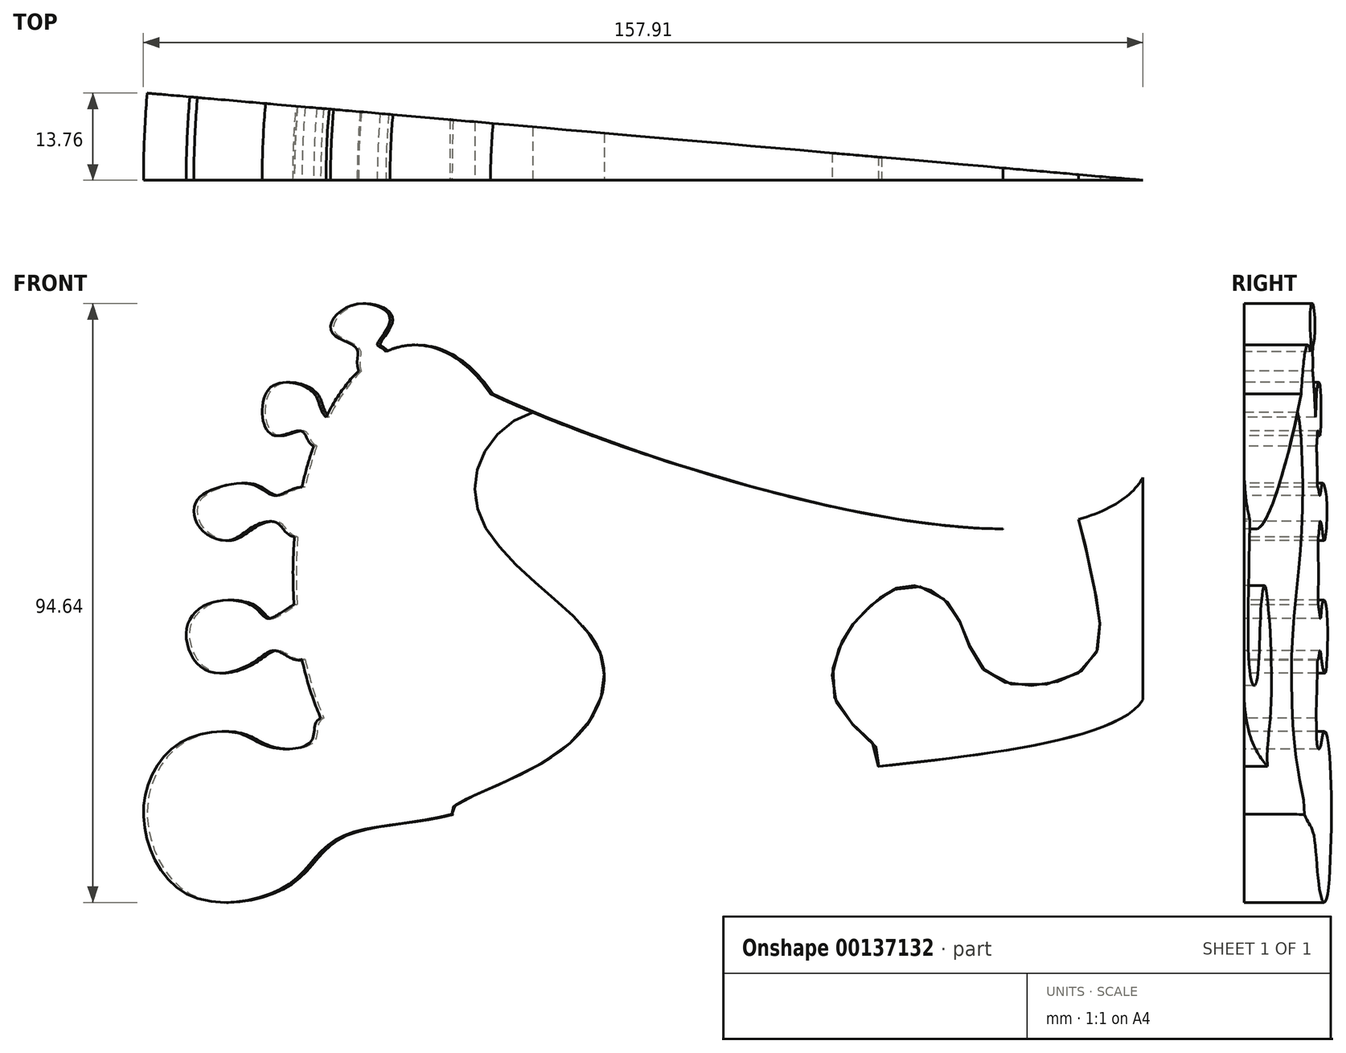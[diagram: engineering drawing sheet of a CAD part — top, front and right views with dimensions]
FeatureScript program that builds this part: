
annotation { "Feature Type Name" : "Feature", "Feature Type Description" : "" }
export const myFeature = defineFeature(function(context is Context, id is Id, definition is map)
    precondition{}
    {
        {
            var Q0;
            Q0=qCreatedBy(makeId("Front.planeOp"),FACE);
            var sketch = newSketch(context, id + "F0", { "sketchPlane" : qUnion([Q0])});
            skLineSegment(sketch, "E0", {"start": v(-61.62, 0) * mm, "end": v(53.38, 0) * mm});
            skLineSegment(sketch, "E1", {"start": v(53.38, 0) * mm, "end": v(53.38, 20) * mm});
            skLineSegment(sketch, "E2", {"start": v(53.38, 20) * mm, "end": v(53.38, -20) * mm});
            skEllipse(sketch, "E3", {"center": v(-61.62, 0) * mm, "majorRadius": 36.06 * mm, "minorRadius": 19.29 * mm, "majorAxis": v(0, 1)});
            skPoint(sketch, "E4.1.internal.snap0", {"position": v(-61.62, 36.06) * mm});
            skFitSpline(sketch, "E4", {"points": [v(-61.62, 36.06) * mm, v(-31.25, 36.06) * mm, v(7.63, 30.97) * mm, v(53.38, 20) * mm, v(35.6, 7.18) * mm, v(-61.62, 36.06) * mm]});
            skFitSpline(sketch, "E5", {"points": [v(-76.53, -22.88) * mm, v(-77.93, -26.43) * mm, v(-84.3, -27.52) * mm, v(-89.38, -25.34) * mm, v(-98.1, -26.43) * mm, v(-103.91, -33.7) * mm, v(-103.55, -43.33) * mm, v(-96.28, -51.32) * mm, v(-81.57, -49.14) * mm, v(-73.75, -41.87) * mm, v(-55.77, -38.06) * mm, v(-50.14, -32.24) * mm, v(-76.53, -22.88) * mm]});
            skFitSpline(sketch, "E6", {"points": [v(-79.48, -13.62) * mm, v(-83.56, -12.26) * mm, v(-87.2, -14.08) * mm, v(-94.65, -15.35) * mm, v(-97.73, -9) * mm, v(-93.74, -4.63) * mm, v(-87.02, -5.36) * mm, v(-84.84, -7.18) * mm, v(-80.73, -4.98) * mm, v(-76.84, -5.54) * mm, v(-79.48, -13.62) * mm]});
            skFitSpline(sketch, "E7", {"points": [v(-80.66, 5.74) * mm, v(-83.38, 7.9) * mm, v(-87.2, 7.36) * mm, v(-91.2, 5.18) * mm, v(-95.74, 7.36) * mm, v(-96.28, 11.17) * mm, v(-92.83, 13.53) * mm, v(-87.02, 13.9) * mm, v(-83.75, 12.26) * mm, v(-79.48, 13.62) * mm, v(-74.3, 10.45) * mm, v(-80.66, 5.74) * mm]});
            skFitSpline(sketch, "E8", {"points": [v(-77.64, 20.1) * mm, v(-79.48, 22.42) * mm, v(-83.38, 21.7) * mm, v(-85.56, 23.89) * mm, v(-84.47, 29.34) * mm, v(-79.48, 29.7) * mm, v(-77.02, 27.52) * mm, v(-75.69, 24.68) * mm, v(-72.12, 21.53) * mm, v(-77.64, 20.1) * mm]});
            skFitSpline(sketch, "E9", {"points": [v(-70.56, 31.96) * mm, v(-70.85, 35.51) * mm, v(-74.84, 38.24) * mm, v(-71.4, 42.42) * mm, v(-65.58, 40.24) * mm, v(-67.58, 36.24) * mm, v(-66.23, 35.02) * mm, v(-64.13, 26.43) * mm, v(-70.56, 31.96) * mm]});
            skFitSpline(sketch, "E10.MirrorCS", {"points": [v(-61.62, -36.06) * mm, v(-31.25, -36.06) * mm, v(7.63, -30.97) * mm, v(53.38, -20) * mm, v(35.6, -7.18) * mm, v(-61.62, -36.06) * mm]});
            skSolve(sketch);
        }
        {
            var Q0;
            {var subQ1=sQuery(id+"F0.wireOp",EDGE,"E3");var subQ10=sQuery(id+"F0.wireOp",EDGE,"E4");var subQ11=makeQuery(id+"F0.imprint","INTERSECT",VERTEX,{"disambiguationData":[OD(0.0)],"derivedFrom":[subQ1,subQ10]});Q0=makeQuery(id+"F0.imprint","IMPRINT",FACE,{"disambiguationData":[TD([[makeQuery(id+"F0.imprint","IMPRINT",EDGE,{"disambiguationData":[TD([[subQ11,-1.0]])],"derivedFrom":subQ1}),1.0]])]});}
            var Q1;
            {var subQ0=sQuery(id+"F0.wireOp",EDGE,"E9");var subQ1=sQuery(id+"F0.wireOp",EDGE,"E3");var subQ2=makeQuery(id+"F0.imprint","INTERSECT",VERTEX,{"disambiguationData":[OD(0.0)],"derivedFrom":[subQ1,subQ0]});Q1=makeQuery(id+"F0.imprint","IMPRINT",FACE,{"disambiguationData":[TD([[makeQuery(id+"F0.imprint","IMPRINT",EDGE,{"disambiguationData":[TD([[subQ2,-1.0]])],"derivedFrom":subQ1}),1.0]])]});}
            var Q2;
            {var subQ0=sQuery(id+"F0.wireOp",EDGE,"E8");var subQ1=sQuery(id+"F0.wireOp",EDGE,"E3");var subQ2=makeQuery(id+"F0.imprint","INTERSECT",VERTEX,{"disambiguationData":[OD(0.0)],"derivedFrom":[subQ1,subQ0]});Q2=makeQuery(id+"F0.imprint","IMPRINT",FACE,{"disambiguationData":[TD([[makeQuery(id+"F0.imprint","IMPRINT",EDGE,{"disambiguationData":[TD([[subQ2,-1.0]])],"derivedFrom":subQ1}),1.0]])]});}
            var Q3;
            {var subQ0=sQuery(id+"F0.wireOp",EDGE,"E7");var subQ1=sQuery(id+"F0.wireOp",EDGE,"E3");var subQ2=makeQuery(id+"F0.imprint","INTERSECT",VERTEX,{"disambiguationData":[OD(0.0)],"derivedFrom":[subQ1,subQ0]});Q3=makeQuery(id+"F0.imprint","IMPRINT",FACE,{"disambiguationData":[TD([[makeQuery(id+"F0.imprint","IMPRINT",EDGE,{"disambiguationData":[TD([[subQ2,-1.0]])],"derivedFrom":subQ1}),1.0]])]});}
            var Q4;
            {var subQ0=sQuery(id+"F0.wireOp",EDGE,"E6");var subQ1=sQuery(id+"F0.wireOp",EDGE,"E3");var subQ2=makeQuery(id+"F0.imprint","INTERSECT",VERTEX,{"disambiguationData":[OD(0.0)],"derivedFrom":[subQ1,subQ0]});Q4=makeQuery(id+"F0.imprint","IMPRINT",FACE,{"disambiguationData":[TD([[makeQuery(id+"F0.imprint","IMPRINT",EDGE,{"disambiguationData":[TD([[subQ2,-1.0]])],"derivedFrom":subQ1}),1.0]])]});}
            var Q5;
            {var subQ0=sQuery(id+"F0.wireOp",EDGE,"E6");var subQ1=sQuery(id+"F0.wireOp",EDGE,"E3");var subQ2=makeQuery(id+"F0.imprint","INTERSECT",VERTEX,{"disambiguationData":[OD(0.0)],"derivedFrom":[subQ1,subQ0]});Q5=makeQuery(id+"F0.imprint","IMPRINT",FACE,{"disambiguationData":[TD([[makeQuery(id+"F0.imprint","IMPRINT",EDGE,{"disambiguationData":[TD([[subQ2,-1.0]])],"derivedFrom":subQ1}),-1.0]])]});}
            var Q6;
            {var subQ0=sQuery(id+"F0.wireOp",EDGE,"E7");var subQ1=sQuery(id+"F0.wireOp",EDGE,"E3");var subQ2=makeQuery(id+"F0.imprint","INTERSECT",VERTEX,{"disambiguationData":[OD(0.0)],"derivedFrom":[subQ1,subQ0]});Q6=makeQuery(id+"F0.imprint","IMPRINT",FACE,{"disambiguationData":[TD([[makeQuery(id+"F0.imprint","IMPRINT",EDGE,{"disambiguationData":[TD([[subQ2,-1.0]])],"derivedFrom":subQ1}),-1.0]])]});}
            var Q7;
            {var subQ0=sQuery(id+"F0.wireOp",EDGE,"E8");var subQ1=sQuery(id+"F0.wireOp",EDGE,"E3");var subQ2=makeQuery(id+"F0.imprint","INTERSECT",VERTEX,{"disambiguationData":[OD(0.0)],"derivedFrom":[subQ1,subQ0]});Q7=makeQuery(id+"F0.imprint","IMPRINT",FACE,{"disambiguationData":[TD([[makeQuery(id+"F0.imprint","IMPRINT",EDGE,{"disambiguationData":[TD([[subQ2,-1.0]])],"derivedFrom":subQ1}),-1.0]])]});}
            var Q8;
            {var subQ0=sQuery(id+"F0.wireOp",EDGE,"E9");var subQ1=sQuery(id+"F0.wireOp",EDGE,"E3");var subQ2=makeQuery(id+"F0.imprint","INTERSECT",VERTEX,{"disambiguationData":[OD(0.0)],"derivedFrom":[subQ1,subQ0]});Q8=makeQuery(id+"F0.imprint","IMPRINT",FACE,{"disambiguationData":[TD([[makeQuery(id+"F0.imprint","IMPRINT",EDGE,{"disambiguationData":[TD([[subQ2,-1.0]])],"derivedFrom":subQ1}),-1.0]])]});}
            var Q9;
            {var subQ0=sQuery(id+"F0.wireOp",EDGE,"E10.MirrorCS");var subQ1=sQuery(id+"F0.wireOp",EDGE,"E3");var subQ2=makeQuery(id+"F0.imprint","INTERSECT",VERTEX,{"disambiguationData":[OD(0.0)],"derivedFrom":[subQ1,subQ0]});Q9=makeQuery(id+"F0.imprint","IMPRINT",FACE,{"disambiguationData":[TD([[makeQuery(id+"F0.imprint","IMPRINT",EDGE,{"disambiguationData":[TD([[subQ2,1.0]])],"derivedFrom":subQ1}),-1.0]])]});}
            var Q10;
            {var subQ0=sQuery(id+"F0.wireOp",EDGE,"E10.MirrorCS");var subQ1=sQuery(id+"F0.wireOp",EDGE,"E3");var subQ2=makeQuery(id+"F0.imprint","INTERSECT",VERTEX,{"disambiguationData":[OD(0.0)],"derivedFrom":[subQ1,subQ0]});Q10=makeQuery(id+"F0.imprint","IMPRINT",FACE,{"disambiguationData":[TD([[makeQuery(id+"F0.imprint","IMPRINT",EDGE,{"disambiguationData":[TD([[subQ2,-1.0]])],"derivedFrom":subQ1}),1.0]])]});}
            var Q11;
            {var subQ0=sQuery(id+"F0.wireOp",EDGE,"E10.MirrorCS");var subQ1=sQuery(id+"F0.wireOp",EDGE,"E3");var subQ2=makeQuery(id+"F0.imprint","INTERSECT",VERTEX,{"disambiguationData":[OD(0.0)],"derivedFrom":[subQ1,subQ0]});Q11=makeQuery(id+"F0.imprint","IMPRINT",FACE,{"disambiguationData":[TD([[makeQuery(id+"F0.imprint","IMPRINT",EDGE,{"disambiguationData":[TD([[subQ2,-1.0]])],"derivedFrom":subQ1}),-1.0]])]});}
            var Q12;
            {var subQ0=sQuery(id+"F0.wireOp",EDGE,"E5");var subQ1=sQuery(id+"F0.wireOp",EDGE,"E3");var subQ2=makeQuery(id+"F0.imprint","INTERSECT",VERTEX,{"disambiguationData":[OD(1.0)],"derivedFrom":[subQ1,subQ0]});Q12=makeQuery(id+"F0.imprint","IMPRINT",FACE,{"disambiguationData":[TD([[makeQuery(id+"F0.imprint","IMPRINT",EDGE,{"disambiguationData":[TD([[subQ2,-1.0]])],"derivedFrom":subQ1}),1.0]])]});}
            var Q13;
            {var subQ0=sQuery(id+"F0.wireOp",EDGE,"E10.MirrorCS");var subQ5=sQuery(id+"F0.wireOp",EDGE,"E2");var subQ8=makeQuery(id+"F0.imprint","INTERSECT",VERTEX,{"disambiguationData":[OD(0.0)],"derivedFrom":[subQ5,subQ0]});Q13=makeQuery(id+"F0.imprint","IMPRINT",FACE,{"disambiguationData":[TD([[makeQuery(id+"F0.imprint","IMPRINT",EDGE,{"disambiguationData":[TD([[subQ8,1.0]])],"derivedFrom":subQ5}),-1.0]])]});}
            var Q14;
            {var subQ0=sQuery(id+"F0.wireOp",EDGE,"E2");var subQ1=sQuery(id+"F0.wireOp",EDGE,"E0");var subQ2=makeQuery(id+"F0.imprint","INTERSECT",VERTEX,{"derivedFrom":[subQ1,subQ0]});Q14=makeQuery(id+"F0.imprint","IMPRINT",FACE,{"disambiguationData":[TD([[makeQuery(id+"F0.imprint","IMPRINT",EDGE,{"disambiguationData":[TD([[subQ2,1.0]])],"derivedFrom":subQ1}),-1.0]])]});}
            var Q15;
            {var subQ0=sQuery(id+"F0.wireOp",EDGE,"E2");var subQ1=sQuery(id+"F0.wireOp",EDGE,"E0");var subQ2=makeQuery(id+"F0.imprint","INTERSECT",VERTEX,{"derivedFrom":[subQ1,subQ0]});Q15=makeQuery(id+"F0.imprint","IMPRINT",FACE,{"disambiguationData":[TD([[makeQuery(id+"F0.imprint","IMPRINT",EDGE,{"disambiguationData":[TD([[subQ2,1.0]])],"derivedFrom":subQ1}),1.0]])]});}
            var Q16;
            {var subQ0=sQuery(id+"F0.wireOp",EDGE,"E4");var subQ1=sQuery(id+"F0.wireOp",EDGE,"E2");var subQ2=makeQuery(id+"F0.imprint","INTERSECT",VERTEX,{"disambiguationData":[OD(0.0)],"derivedFrom":[subQ1,subQ0]});Q16=makeQuery(id+"F0.imprint","IMPRINT",FACE,{"disambiguationData":[TD([[makeQuery(id+"F0.imprint","IMPRINT",EDGE,{"disambiguationData":[TD([[subQ2,-1.0]])],"derivedFrom":subQ1}),-1.0]])]});}
            var Q17;
            {var subQ0=sQuery(id+"F0.wireOp",EDGE,"E10.MirrorCS");var subQ1=sQuery(id+"F0.wireOp",EDGE,"E3");var subQ2=makeQuery(id+"F0.imprint","INTERSECT",VERTEX,{"disambiguationData":[OD(0.0)],"derivedFrom":[subQ1,subQ0]});Q17=makeQuery(id+"F0.imprint","IMPRINT",FACE,{"disambiguationData":[TD([[makeQuery(id+"F0.imprint","IMPRINT",EDGE,{"disambiguationData":[TD([[subQ2,1.0]])],"derivedFrom":subQ1}),1.0]])]});}
            var Q18;
            {var subQ0=sQuery(id+"F0.wireOp",EDGE,"E4");var subQ1=sQuery(id+"F0.wireOp",EDGE,"E3");var subQ2=makeQuery(id+"F0.imprint","INTERSECT",VERTEX,{"disambiguationData":[OD(0.0)],"derivedFrom":[subQ1,subQ0]});Q18=makeQuery(id+"F0.imprint","IMPRINT",FACE,{"disambiguationData":[TD([[makeQuery(id+"F0.imprint","IMPRINT",EDGE,{"disambiguationData":[TD([[subQ2,1.0]])],"derivedFrom":subQ1}),1.0]])]});}
            var Q19;
            Q19=sQuery(id+"F0.wireOp",EDGE,"E2");
            revolve(context, id + "F1", {"entities" : qUnion([Q0, Q1, Q2, Q3, Q4, Q5, Q6, Q7, Q8, Q9, Q10, Q11, Q12, Q13, Q14, Q15, Q16, Q17, Q18]), "axis" : qUnion([Q19]), "revolveType" : RevolveType.ONE_DIRECTION, "angle" : 5 * degree});
        }
        {
            var Q0;
            Q0=makeQuery(id+"F1.opRevolve","CAP_FACE",FACE,{"disambiguationData":[OSD([sQuery(id+"F0.wireOp",EDGE,"E2"),sQuery(id+"F0.wireOp",EDGE,"E3"),sQuery(id+"F0.wireOp",EDGE,"E4"),sQuery(id+"F0.wireOp",EDGE,"E5"),sQuery(id+"F0.wireOp",EDGE,"E6"),sQuery(id+"F0.wireOp",EDGE,"E7"),sQuery(id+"F0.wireOp",EDGE,"E8"),sQuery(id+"F0.wireOp",EDGE,"E9"),sQuery(id+"F0.wireOp",EDGE,"E10.MirrorCS")])],"isStart":true});
            var sketch = newSketch(context, id + "F2", { "sketchPlane" : qUnion([Q0])});
            skFitSpline(sketch, "E11", {"points": [v(-55.77, -38.06) * mm, v(-39.65, -28.8) * mm, v(-32.02, -13.72) * mm, v(-41.28, -2.63) * mm, v(-51.28, 8.81) * mm, v(-50.91, 18.62) * mm, v(-42.56, 25.52) * mm, v(-28.93, 22.62) * mm, v(-10.77, 17.9) * mm, v(20.3, 19.71) * mm, v(39.2, 15.9) * mm, v(45.19, 0) * mm, v(44.82, -14.44) * mm, v(29.74, -16.44) * mm, v(23.93, -6.63) * mm, v(19.2, -2.45) * mm, v(14.67, -2.27) * mm, v(9.76, -5.72) * mm, v(6.31, -9.9) * mm, v(5.4, -21.35) * mm, v(11.62, -30.53) * mm, v(-55.77, -38.06) * mm]});
            skSolve(sketch);
        }
        {
            var Q0;
            {var subQ0=sQuery(id+"F2.wireOp",EDGE,"E11");var subQ1=makeQuery(id+"F1.opRevolve","CAP_EDGE",EDGE,{"disambiguationData":[OSD([sQuery(id+"F0.wireOp",EDGE,"E10.MirrorCS")])],"isStart":true});var subQ3=makeQuery(id+"F2.imprint","INTERSECT",VERTEX,{"derivedFrom":[subQ1,subQ0]});Q0=makeQuery(id+"F2.imprint","IMPRINT",FACE,{"disambiguationData":[TD([[makeQuery(id+"F2.imprint","IMPRINT",EDGE,{"disambiguationData":[TD([[subQ3,1.0]])],"derivedFrom":subQ0}),-1.0]])]});}
            var Q1;
            {var subQ0=sQuery(id+"F2.wireOp",EDGE,"E11");var subQ1=makeQuery(id+"F1.opRevolve","CAP_EDGE",EDGE,{"disambiguationData":[OSD([sQuery(id+"F0.wireOp",EDGE,"E10.MirrorCS")])],"isStart":true});var subQ3=makeQuery(id+"F2.imprint","INTERSECT",VERTEX,{"derivedFrom":[subQ1,subQ0]});Q1=makeQuery(id+"F2.imprint","IMPRINT",FACE,{"disambiguationData":[TD([[makeQuery(id+"F2.imprint","IMPRINT",EDGE,{"disambiguationData":[TD([[subQ3,-1.0]])],"derivedFrom":subQ0}),-1.0]])]});}
            extrude(context, id + "F3", {"entities" : qUnion([Q0, Q1]), "operationType" : NewBodyOperationType.REMOVE, "oppositeDirection" : true, "depth" : 25 * mm});
        }
    });
